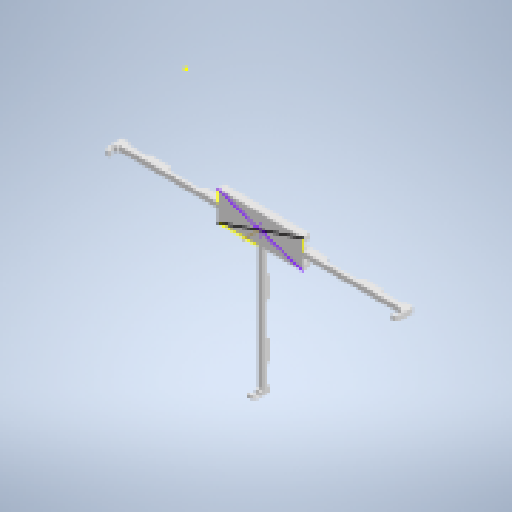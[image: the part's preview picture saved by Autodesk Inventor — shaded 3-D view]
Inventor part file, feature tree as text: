
AUTODESK INVENTOR PART (.ipt)
format: ipt  version: 2023 (Build 270158000, 158)  size: 388,096 bytes
history: native  units: mm
features: sketch x12, extrude x11, projected_geometry x8, other x6, fillet x2, pattern_circular x1
ambient origin geometry x8: Origin, YZ Plane, XZ Plane, XY Plane, X Axis, Y Axis, Z Axis, Center Point
bodies: Solide1 (feature_tree)
feature tree (40):
  extrude  "Extrusion1"  Depth=0.5mm
  extrude  "Extrusion2"  Depth=50.0mm
  extrude  "Extrusion3"  Depth=3.0mm
  extrude  "Extrusion4"  Depth=3.0mm
  sketch  "Esquisse5"
  extrude  "Extrusion5"  Depth=2.9mm TaperAngle=0.0deg
  extrude  "Extrusion6"  Depth=82.5mm
  extrude  "Extrusion7"  Depth=82.5mm
  extrude  "Extrusion8"  Depth=1.5mm
  extrude  "Extrusion9"  Depth=1.5mm
  fillet  "Congé1"  Radius=1.5mm
  extrude  "Extrusion10"  Depth=3.0mm
  sketch  "Esquisse11"
  other  "Axe de construction1"
  pattern_circular  "Réseau circulaire1"  [2 undecoded]
  extrude  "Extrusion11"  Depth=1.5mm TaperAngle=0.0deg
  fillet  "Congé2"  Radius=1.5mm
  sketch  "Esquisse1"
  other  "Référence1"
  other  "Référence2"
  sketch  "Esquisse2"
  sketch  "Esquisse3"
  sketch  "Esquisse4"
  projected_geometry  "Boucle projetée1"
  projected_geometry  "Boucle projetée2"
  projected_geometry  "Boucle projetée3"
  projected_geometry  "Boucle projetée4"
  projected_geometry  "Boucle projetée5"
  sketch  "Esquisse6"
  sketch  "Esquisse7"
  sketch  "Esquisse8"
  projected_geometry  "Boucle projetée6"
  sketch  "Esquisse9"
  sketch  "Esquisse10"
  sketch  "Esquisse12"
  projected_geometry  "Boucle projetée7"
  projected_geometry  "Boucle projetée8"
  other  "<userpath>\Desktop\PE-SM\3D\Ensemble.iam"
  other  "Ensemble.iam"
  other  "PE:1"
note: 2 required parameter values undecoded (feature->parameter linkage not recoverable at this tier; creation-order binding heuristic only, values carry confidence <= 0.55)
